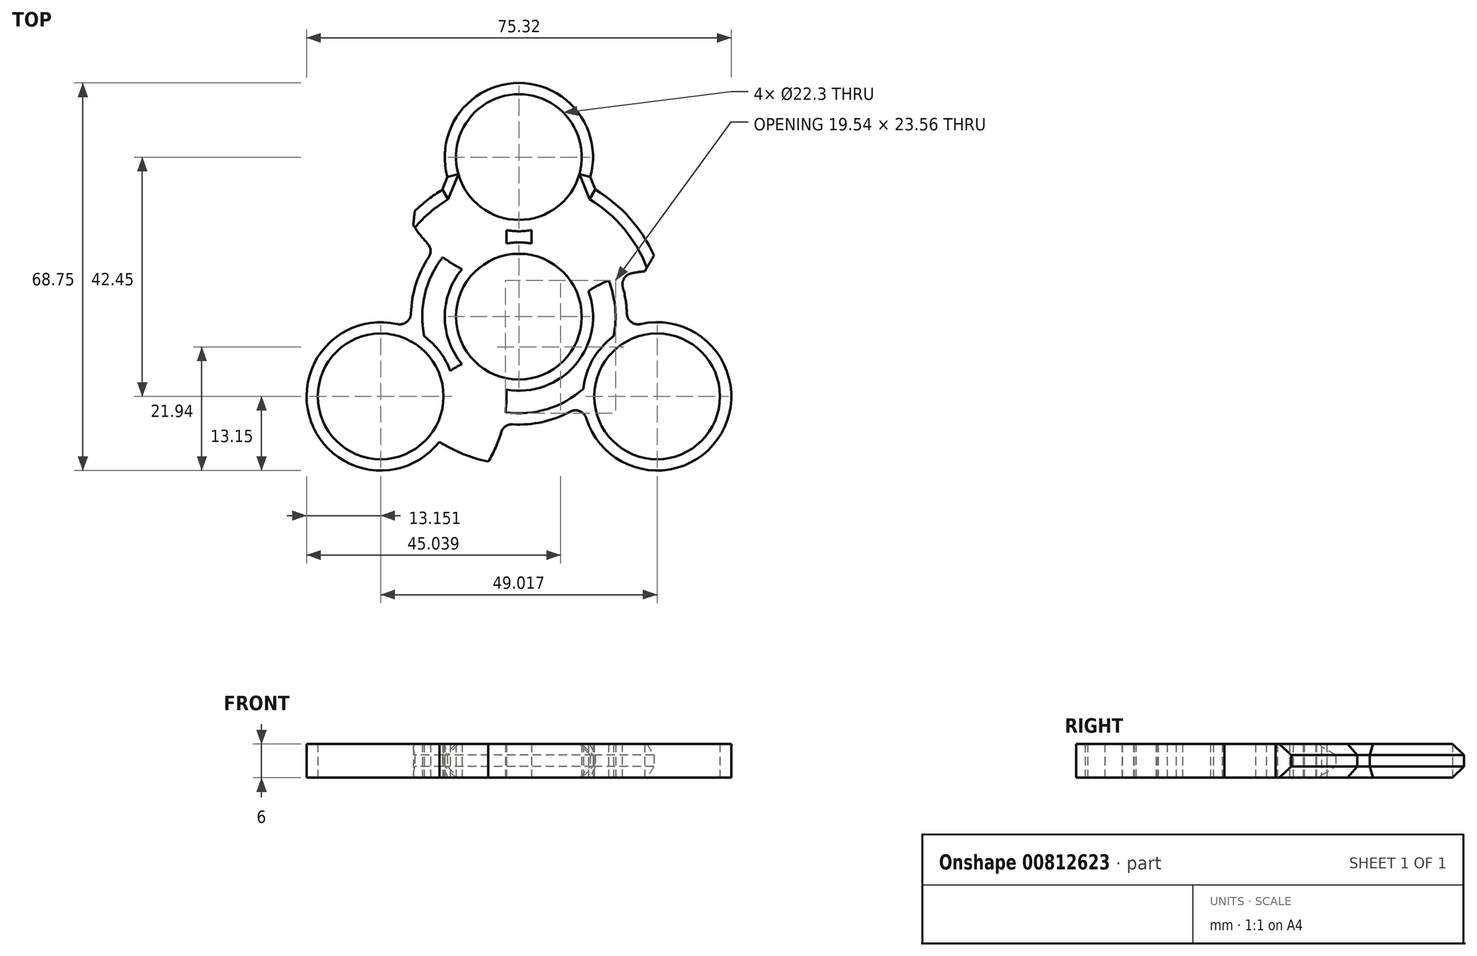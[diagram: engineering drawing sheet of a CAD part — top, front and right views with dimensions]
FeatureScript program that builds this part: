
annotation { "Feature Type Name" : "Feature", "Feature Type Description" : "" }
export const myFeature = defineFeature(function(context is Context, id is Id, definition is map)
    precondition{}
    {
        {
            assignVariable(context, id + "F0", {"name" : "t", "anyValue" : 2 * mm});
        }
        {
            var Q0;
            Q0=qCreatedBy(makeId("Top.planeOp"),FACE);
            var sketch = newSketch(context, id + "F1", { "sketchPlane" : qUnion([Q0])});
            skCircle(sketch, "E0", {"center": v(0, 0) * mm, "radius": 11.15 * mm});
            skCircle(sketch, "E1", {"center": v(0, 28.3) * mm, "radius": 11.15 * mm});
            skCircle(sketch, "E2.1.0", {"center": v(-24.5, -14.15) * mm, "radius": 11.15 * mm});
            skCircle(sketch, "E2.2.0", {"center": v(24.5, -14.15) * mm, "radius": 11.15 * mm});
            skSolve(sketch);
        }
        {
            var Q0;
            Q0=qCreatedBy(makeId("Top.planeOp"),FACE);
            var sketch = newSketch(context, id + "F2", { "sketchPlane" : qUnion([Q0])});
            skCircle(sketch, "E3.0", {"center": v(0, 28.3) * mm, "radius": 13.15 * mm});
            skCircle(sketch, "E4.0", {"center": v(-24.5, -14.15) * mm, "radius": 13.15 * mm});
            skCircle(sketch, "E5.0", {"center": v(0, 0) * mm, "radius": 13.15 * mm});
            skCircle(sketch, "E6.0", {"center": v(24.5, -14.15) * mm, "radius": 13.15 * mm});
            skSolve(sketch);
        }
        {
            var Q0;
            Q0=qCreatedBy(makeId("Top.planeOp"),FACE);
            var sketch = newSketch(context, id + "F3", { "sketchPlane" : qUnion([Q0])});
            skCircle(sketch, "E7", {"center": v(0, 0) * mm, "radius": 28.3 * mm});
            skCircle(sketch, "E8.0", {"center": v(0, 0) * mm, "radius": 26.3 * mm});
            skSolve(sketch);
        }
        {
            var Q0;
            Q0=qCreatedBy(makeId("Top.planeOp"),FACE);
            var sketch = newSketch(context, id + "F4", { "sketchPlane" : qUnion([Q0])});
            skArc(sketch, "E9", {"start": v(19.56, 17.58) * mm, "mid": v(0, 6) * mm, "end": v(-19.56, 17.58) * mm});
            skArc(sketch, "E10.1.0", {"start": v(-5.45, 25.73) * mm, "mid": v(-5.2, 3) * mm, "end": v(-25, -8.14) * mm});
            skArc(sketch, "E10.2.0", {"start": v(-25, 8.14) * mm, "mid": v(-5.2, -3) * mm, "end": v(-5.45, -25.73) * mm});
            skArc(sketch, "E10.3.0", {"start": v(-19.56, -17.58) * mm, "mid": v(0, -6) * mm, "end": v(19.56, -17.58) * mm});
            skArc(sketch, "E10.4.0", {"start": v(5.45, -25.73) * mm, "mid": v(5.2, -3) * mm, "end": v(25, 8.14) * mm});
            skArc(sketch, "E10.5.0", {"start": v(25, -8.14) * mm, "mid": v(5.2, 3) * mm, "end": v(5.45, 25.73) * mm});
            skPoint(sketch, "E10.center", {"position": v(0, 0) * mm});
            skCircle(sketch, "E11", {"center": v(0, 0) * mm, "radius": 26.3 * mm});
            skSolve(sketch);
        }
        {
            var Q0;
            Q0=qCreatedBy(makeId("Top.planeOp"),FACE);
            var sketch = newSketch(context, id + "F5", { "sketchPlane" : qUnion([Q0])});
            skCircle(sketch, "E12", {"center": v(0, 0) * mm, "radius": 17.15 * mm});
            skCircle(sketch, "E13.0", {"center": v(0, 0) * mm, "radius": 19.15 * mm});
            skSolve(sketch);
        }
        {
            var Q0;
            Q0 = qSketchRegion(id + "F5", true);
            extrude(context, id + "F6", {"entities" : qUnion([Q0]), "depth" : 6 * mm, "offsetDistance" : 25 * mm});
        }
        {
            var Q0;
            {var subQ0=sQuery(id+"F4.wireOp",EDGE,"E11");var subQ1=sQuery(id+"F4.wireOp",EDGE,"E9");var subQ2=makeQuery(id+"F4.imprint","INTERSECT",VERTEX,{"disambiguationData":[OD(1.0)],"derivedFrom":[subQ1,subQ0]});Q0=makeQuery(id+"F4.imprint","IMPRINT",FACE,{"disambiguationData":[TD([[makeQuery(id+"F4.imprint","IMPRINT",EDGE,{"disambiguationData":[TD([[subQ2,1.0]])],"derivedFrom":subQ1}),1.0]])]});}
            var Q1;
            {var subQ0=sQuery(id+"F4.wireOp",EDGE,"E11");var subQ1=sQuery(id+"F4.wireOp",EDGE,"E10.1.0");var subQ2=makeQuery(id+"F4.imprint","INTERSECT",VERTEX,{"disambiguationData":[OD(1.0)],"derivedFrom":[subQ1,subQ0]});Q1=makeQuery(id+"F4.imprint","IMPRINT",FACE,{"disambiguationData":[TD([[makeQuery(id+"F4.imprint","IMPRINT",EDGE,{"disambiguationData":[TD([[subQ2,1.0]])],"derivedFrom":subQ1}),1.0]])]});}
            var Q2;
            {var subQ0=sQuery(id+"F4.wireOp",EDGE,"E11");var subQ1=sQuery(id+"F4.wireOp",EDGE,"E10.2.0");var subQ2=makeQuery(id+"F4.imprint","INTERSECT",VERTEX,{"disambiguationData":[OD(1.0)],"derivedFrom":[subQ1,subQ0]});Q2=makeQuery(id+"F4.imprint","IMPRINT",FACE,{"disambiguationData":[TD([[makeQuery(id+"F4.imprint","IMPRINT",EDGE,{"disambiguationData":[TD([[subQ2,1.0]])],"derivedFrom":subQ1}),1.0]])]});}
            var Q3;
            {var subQ0=sQuery(id+"F4.wireOp",EDGE,"E11");var subQ1=sQuery(id+"F4.wireOp",EDGE,"E10.3.0");var subQ2=makeQuery(id+"F4.imprint","INTERSECT",VERTEX,{"disambiguationData":[OD(1.0)],"derivedFrom":[subQ1,subQ0]});Q3=makeQuery(id+"F4.imprint","IMPRINT",FACE,{"disambiguationData":[TD([[makeQuery(id+"F4.imprint","IMPRINT",EDGE,{"disambiguationData":[TD([[subQ2,1.0]])],"derivedFrom":subQ1}),1.0]])]});}
            var Q4;
            {var subQ0=sQuery(id+"F4.wireOp",EDGE,"E11");var subQ1=sQuery(id+"F4.wireOp",EDGE,"E9");var subQ2=makeQuery(id+"F4.imprint","INTERSECT",VERTEX,{"disambiguationData":[OD(0.0)],"derivedFrom":[subQ1,subQ0]});Q4=makeQuery(id+"F4.imprint","IMPRINT",FACE,{"disambiguationData":[TD([[makeQuery(id+"F4.imprint","IMPRINT",EDGE,{"disambiguationData":[TD([[subQ2,-1.0]])],"derivedFrom":subQ1}),1.0]])]});}
            var Q5;
            {var subQ0=sQuery(id+"F4.wireOp",EDGE,"E10.5.0");var subQ1=sQuery(id+"F4.wireOp",EDGE,"E9");var subQ2=makeQuery(id+"F4.imprint","INTERSECT",VERTEX,{"derivedFrom":[subQ1,subQ0]});Q5=makeQuery(id+"F4.imprint","IMPRINT",FACE,{"disambiguationData":[TD([[makeQuery(id+"F4.imprint","IMPRINT",EDGE,{"disambiguationData":[TD([[subQ2,-1.0]])],"derivedFrom":subQ1}),-1.0]])]});}
            var Q6;
            Q6=makeQuery(id+"F2.imprint","IMPRINT",FACE,{"disambiguationData":[TD([[makeQuery(id+"F2.imprint","IMPRINT",EDGE,{"derivedFrom":sQuery(id+"F2.wireOp",EDGE,"E5.0")}),1.0]])]});
            var Q7;
            Q7=makeQuery(id+"F2.imprint","IMPRINT",FACE,{"disambiguationData":[TD([[makeQuery(id+"F2.imprint","IMPRINT",EDGE,{"derivedFrom":sQuery(id+"F2.wireOp",EDGE,"E4.0")}),1.0]])]});
            var Q8;
            Q8=makeQuery(id+"F2.imprint","IMPRINT",FACE,{"disambiguationData":[TD([[makeQuery(id+"F2.imprint","IMPRINT",EDGE,{"derivedFrom":sQuery(id+"F2.wireOp",EDGE,"E6.0")}),1.0]])]});
            var Q9;
            Q9=makeQuery(id+"F2.imprint","IMPRINT",FACE,{"disambiguationData":[TD([[makeQuery(id+"F2.imprint","IMPRINT",EDGE,{"derivedFrom":sQuery(id+"F2.wireOp",EDGE,"E3.0")}),1.0]])]});
            extrude(context, id + "F7", {"entities" : qUnion([Q0, Q1, Q2, Q3, Q4, Q5, Q6, Q7, Q8, Q9]), "operationType" : NewBodyOperationType.ADD, "depth" : 6 * mm, "offsetDistance" : 25 * mm});
        }
        {
            var Q0;
            Q0 = qSketchRegion(id + "F1", true);
            extrude(context, id + "F8", {"entities" : qUnion([Q0]), "operationType" : NewBodyOperationType.REMOVE, "endBound" : BoundingType.THROUGH_ALL, "depth" : 25 * mm, "offsetDistance" : 25 * mm});
        }
        {
            var Q0;
            Q0=makeQuery(id+"F7.boolean.opBoolean","INTERSECT",EDGE,{"disambiguationData":[OD(1.0)],"derivedFrom":[makeQuery(id+"F6.opExtrude","SWEPT_FACE",FACE,{"disambiguationData":[OSD([sQuery(id+"F5.wireOp",EDGE,"E13.0")])]}),makeQuery(id+"F7.opExtrude","SWEPT_FACE",FACE,{"disambiguationData":[OSD([sQuery(id+"F2.wireOp",EDGE,"E4.0")])]})]});
            var Q1;
            {var subQ0=sQuery(id+"F4.wireOp",EDGE,"E10.2.0");Q1=makeQuery(id+"F7.boolean.opBoolean","INTERSECT",EDGE,{"derivedFrom":[makeQuery(id+"F6.opExtrude","SWEPT_FACE",FACE,{"disambiguationData":[OSD([sQuery(id+"F5.wireOp",EDGE,"E13.0")])]}),makeQuery(id+"F7.opExtrude","SWEPT_FACE",FACE,{"disambiguationData":[OSD([subQ0]),TDD([makeQuery(id+"F4.imprint","IMPRINT",EDGE,{"disambiguationData":[TD([[makeQuery(id+"F4.imprint","INTERSECT",VERTEX,{"disambiguationData":[OD(1.0)],"derivedFrom":[subQ0,sQuery(id+"F4.wireOp",EDGE,"E11")]}),1.0]])],"derivedFrom":subQ0})])]})]});}
            var Q2;
            {var subQ0=sQuery(id+"F4.wireOp",EDGE,"E10.4.0");Q2=makeQuery(id+"F7.boolean.opBoolean","INTERSECT",EDGE,{"derivedFrom":[makeQuery(id+"F6.opExtrude","SWEPT_FACE",FACE,{"disambiguationData":[OSD([sQuery(id+"F5.wireOp",EDGE,"E13.0")])]}),makeQuery(id+"F7.opExtrude","SWEPT_FACE",FACE,{"disambiguationData":[OSD([subQ0]),TDD([makeQuery(id+"F4.imprint","IMPRINT",EDGE,{"disambiguationData":[TD([[makeQuery(id+"F4.imprint","INTERSECT",VERTEX,{"disambiguationData":[OD(0.0)],"derivedFrom":[subQ0,sQuery(id+"F4.wireOp",EDGE,"E11")]}),-1.0]])],"derivedFrom":subQ0})])]})]});}
            var Q3;
            Q3=makeQuery(id+"F7.boolean.opBoolean","INTERSECT",EDGE,{"disambiguationData":[OD(0.0)],"derivedFrom":[makeQuery(id+"F6.opExtrude","SWEPT_FACE",FACE,{"disambiguationData":[OSD([sQuery(id+"F5.wireOp",EDGE,"E13.0")])]}),makeQuery(id+"F7.opExtrude","SWEPT_FACE",FACE,{"disambiguationData":[OSD([sQuery(id+"F2.wireOp",EDGE,"E6.0")])]})]});
            var Q4;
            Q4=makeQuery(id+"F7.boolean.opBoolean","INTERSECT",EDGE,{"disambiguationData":[OD(1.0)],"derivedFrom":[makeQuery(id+"F6.opExtrude","SWEPT_FACE",FACE,{"disambiguationData":[OSD([sQuery(id+"F5.wireOp",EDGE,"E13.0")])]}),makeQuery(id+"F7.opExtrude","SWEPT_FACE",FACE,{"disambiguationData":[OSD([sQuery(id+"F2.wireOp",EDGE,"E6.0")])]})]});
            var Q5;
            {var subQ0=sQuery(id+"F4.wireOp",EDGE,"E10.4.0");Q5=makeQuery(id+"F7.boolean.opBoolean","INTERSECT",EDGE,{"derivedFrom":[makeQuery(id+"F6.opExtrude","SWEPT_FACE",FACE,{"disambiguationData":[OSD([sQuery(id+"F5.wireOp",EDGE,"E13.0")])]}),makeQuery(id+"F7.opExtrude","SWEPT_FACE",FACE,{"disambiguationData":[OSD([subQ0]),TDD([makeQuery(id+"F4.imprint","IMPRINT",EDGE,{"disambiguationData":[TD([[makeQuery(id+"F4.imprint","INTERSECT",VERTEX,{"disambiguationData":[OD(1.0)],"derivedFrom":[subQ0,sQuery(id+"F4.wireOp",EDGE,"E11")]}),1.0]])],"derivedFrom":subQ0})])]})]});}
            var Q6;
            {var subQ0=sQuery(id+"F4.wireOp",EDGE,"E9");Q6=makeQuery(id+"F7.boolean.opBoolean","INTERSECT",EDGE,{"derivedFrom":[makeQuery(id+"F6.opExtrude","SWEPT_FACE",FACE,{"disambiguationData":[OSD([sQuery(id+"F5.wireOp",EDGE,"E13.0")])]}),makeQuery(id+"F7.opExtrude","SWEPT_FACE",FACE,{"disambiguationData":[OSD([subQ0]),TDD([makeQuery(id+"F4.imprint","IMPRINT",EDGE,{"disambiguationData":[TD([[makeQuery(id+"F4.imprint","INTERSECT",VERTEX,{"disambiguationData":[OD(0.0)],"derivedFrom":[subQ0,sQuery(id+"F4.wireOp",EDGE,"E11")]}),-1.0]])],"derivedFrom":subQ0})])]})]});}
            var Q7;
            Q7=makeQuery(id+"F7.boolean.opBoolean","INTERSECT",EDGE,{"disambiguationData":[OD(0.0)],"derivedFrom":[makeQuery(id+"F6.opExtrude","SWEPT_FACE",FACE,{"disambiguationData":[OSD([sQuery(id+"F5.wireOp",EDGE,"E13.0")])]}),makeQuery(id+"F7.opExtrude","SWEPT_FACE",FACE,{"disambiguationData":[OSD([sQuery(id+"F2.wireOp",EDGE,"E3.0")])]})]});
            var Q8;
            Q8=makeQuery(id+"F7.boolean.opBoolean","INTERSECT",EDGE,{"disambiguationData":[OD(1.0)],"derivedFrom":[makeQuery(id+"F6.opExtrude","SWEPT_FACE",FACE,{"disambiguationData":[OSD([sQuery(id+"F5.wireOp",EDGE,"E13.0")])]}),makeQuery(id+"F7.opExtrude","SWEPT_FACE",FACE,{"disambiguationData":[OSD([sQuery(id+"F2.wireOp",EDGE,"E3.0")])]})]});
            var Q9;
            {var subQ0=sQuery(id+"F4.wireOp",EDGE,"E9");Q9=makeQuery(id+"F7.boolean.opBoolean","INTERSECT",EDGE,{"derivedFrom":[makeQuery(id+"F6.opExtrude","SWEPT_FACE",FACE,{"disambiguationData":[OSD([sQuery(id+"F5.wireOp",EDGE,"E13.0")])]}),makeQuery(id+"F7.opExtrude","SWEPT_FACE",FACE,{"disambiguationData":[OSD([subQ0]),TDD([makeQuery(id+"F4.imprint","IMPRINT",EDGE,{"disambiguationData":[TD([[makeQuery(id+"F4.imprint","INTERSECT",VERTEX,{"disambiguationData":[OD(1.0)],"derivedFrom":[subQ0,sQuery(id+"F4.wireOp",EDGE,"E11")]}),1.0]])],"derivedFrom":subQ0})])]})]});}
            var Q10;
            {var subQ0=sQuery(id+"F4.wireOp",EDGE,"E10.2.0");Q10=makeQuery(id+"F7.boolean.opBoolean","INTERSECT",EDGE,{"derivedFrom":[makeQuery(id+"F6.opExtrude","SWEPT_FACE",FACE,{"disambiguationData":[OSD([sQuery(id+"F5.wireOp",EDGE,"E13.0")])]}),makeQuery(id+"F7.opExtrude","SWEPT_FACE",FACE,{"disambiguationData":[OSD([subQ0]),TDD([makeQuery(id+"F4.imprint","IMPRINT",EDGE,{"disambiguationData":[TD([[makeQuery(id+"F4.imprint","INTERSECT",VERTEX,{"disambiguationData":[OD(0.0)],"derivedFrom":[subQ0,sQuery(id+"F4.wireOp",EDGE,"E11")]}),-1.0]])],"derivedFrom":subQ0})])]})]});}
            var Q11;
            Q11=makeQuery(id+"F7.boolean.opBoolean","INTERSECT",EDGE,{"disambiguationData":[OD(0.0)],"derivedFrom":[makeQuery(id+"F6.opExtrude","SWEPT_FACE",FACE,{"disambiguationData":[OSD([sQuery(id+"F5.wireOp",EDGE,"E13.0")])]}),makeQuery(id+"F7.opExtrude","SWEPT_FACE",FACE,{"disambiguationData":[OSD([sQuery(id+"F2.wireOp",EDGE,"E4.0")])]})]});
            fillet(context, id + "F9", {"entities" : qUnion([Q0, Q1, Q2, Q3, Q4, Q5, Q6, Q7, Q8, Q9, Q10, Q11]), "radius" : getVariable(context, 't'), "allowEdgeOverflow" : false});
        }
        {
            var Q0;
            {var subQ0=sQuery(id+"F4.wireOp",EDGE,"E11");Q0=makeQuery(id+"F7.opExtrude","SWEPT_FACE",FACE,{"disambiguationData":[OSD([subQ0]),TDD([makeQuery(id+"F4.imprint","IMPRINT",EDGE,{"disambiguationData":[TD([[makeQuery(id+"F4.imprint","INTERSECT",VERTEX,{"disambiguationData":[OD(1.0)],"derivedFrom":[sQuery(id+"F4.wireOp",EDGE,"E10.2.0"),subQ0]}),-1.0]])],"derivedFrom":subQ0})])]});}
            var Q1;
            {var subQ0=sQuery(id+"F4.wireOp",EDGE,"E11");Q1=makeQuery(id+"F7.opExtrude","SWEPT_FACE",FACE,{"disambiguationData":[OSD([subQ0]),TDD([makeQuery(id+"F4.imprint","IMPRINT",EDGE,{"disambiguationData":[TD([[makeQuery(id+"F4.imprint","INTERSECT",VERTEX,{"disambiguationData":[OD(0.0)],"derivedFrom":[sQuery(id+"F4.wireOp",EDGE,"E9"),subQ0]}),1.0]])],"derivedFrom":subQ0})])]});}
            var Q2;
            {var subQ0=sQuery(id+"F4.wireOp",EDGE,"E11");Q2=makeQuery(id+"F7.opExtrude","SWEPT_FACE",FACE,{"disambiguationData":[OSD([subQ0]),TDD([makeQuery(id+"F4.imprint","IMPRINT",EDGE,{"disambiguationData":[TD([[makeQuery(id+"F4.imprint","INTERSECT",VERTEX,{"disambiguationData":[OD(1.0)],"derivedFrom":[sQuery(id+"F4.wireOp",EDGE,"E9"),subQ0]}),-1.0]])],"derivedFrom":subQ0})])]});}
            chamfer(context, id + "F10", {"entities" : qUnion([Q0, Q1, Q2]), "width" : getVariable(context, 't'), "tangentPropagation" : true});
        }
    });
